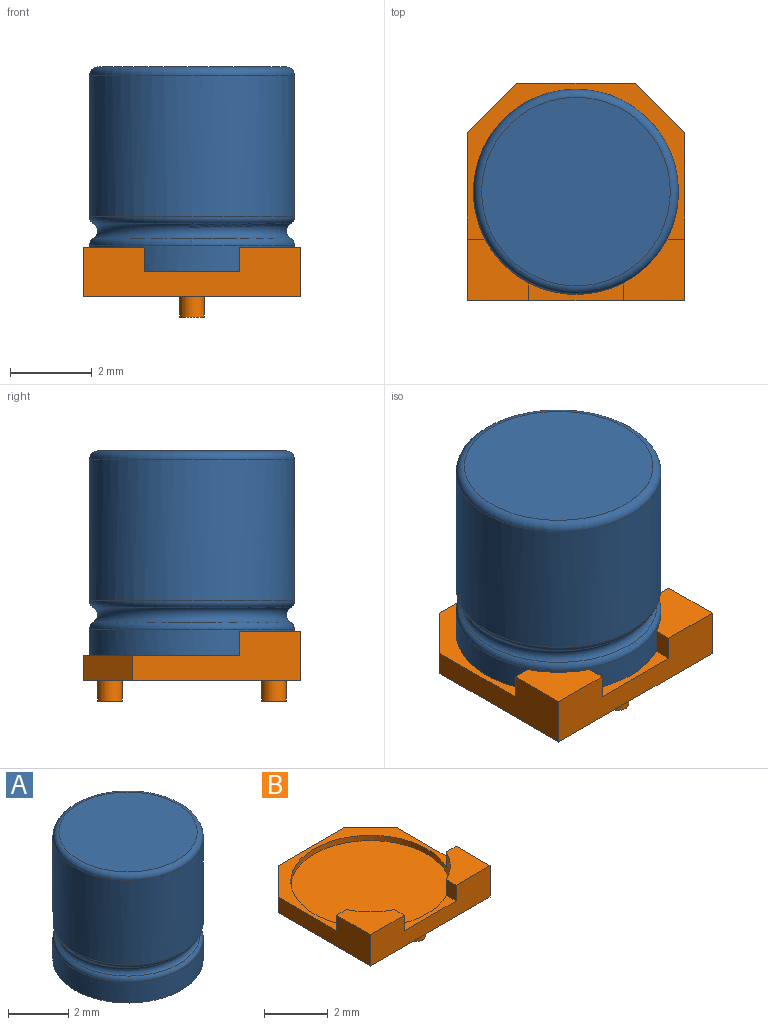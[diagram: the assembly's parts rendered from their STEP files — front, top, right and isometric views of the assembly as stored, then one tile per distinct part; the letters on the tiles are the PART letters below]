
ASSEMBLY  parts=2 mates=1
PART A: 8 faces, bbox 5.4x5.4x5.2 mm
  f0: plane 5x5mm, normal (0,0,-1), area 19.6mm2, adj f1
  f1: cylinder r=2.5mm len=5mm, axis (0,0,1), area 13.4mm2, adj f0,f5
  f2: torus R=2.5mm, axis (0,0,1), area 6.1mm2, adj f5,f6
  f3: cylinder r=2.5mm len=5mm, axis (0,0,1), area 54.2mm2, adj f6,f7
  f4: plane 4.6x4.6mm, normal (0,0,1), area 16.6mm2, adj f7
  f5: torus R=2.3mm, axis (0,0,-1), area 3.2mm2, adj f1,f2
  f6: torus R=2.3mm, axis (0,0,-1), area 3.2mm2, adj f2,f3
  f7: torus R=2.3mm, axis (0,0,1), area 4.8mm2, adj f3,f4
PART B: 21 faces, bbox 5.3x5.3x1.7 mm
  f0: plane 5.3x3.8mm, normal (0,0,1), area 3.3mm2, adj f2,f3,f4,f6,f7,f9,f11,f15
  f1: plane 2.3x0.43mm, normal (0,0,1), area 0.6mm2, adj f5,f9,f12,f14
  f2: plane 2.9x0.6mm, normal (0,1,0), area 1.7mm2, adj f0,f3,f7,f8
  f3: plane 1.2x1.2mm, normal (-0.71,0.71,0), area 1mm2, adj f0,f2,f4,f8
  f4: plane 4.1x1.2mm, normal (-1,0,0), area 3.4mm2, adj f0,f3,f5,f8,f11,f13
  f5: plane 5.3x1.2mm, normal (0,-1,0), area 5mm2, adj f1,f4,f6,f8,f12,f13,f14,f16
  f6: plane 4.1x1.2mm, normal (1,0,0), area 3.4mm2, adj f0,f5,f7,f8,f15,f16
  f7: plane 1.2x1.2mm, normal (0.71,0.71,0), area 1mm2, adj f0,f2,f6,f8
  f8: plane 5.3x5.3mm, normal (0,0,-1), area 26.1mm2, adj f2,f3,f4,f5,f6,f7,f17,f19
  f9: cylinder r=2.5mm len=5mm, axis (0,0,1), area 5mm2, adj f0,f1,f10,f11,f12,f13,f14,f15
  f10: plane 5x5mm, normal (0,0,1), area 19.6mm2, adj f9
  f11: plane 0.6x0.43mm, normal (0,1,0), area 0.3mm2, adj f0,f4,f9,f13
  f12: plane 0.6x0.43mm, normal (1,0,0), area 0.3mm2, adj f1,f5,f9,f13
  f13: plane 1.5x1.5mm, normal (0,0,1), area 1.6mm2, adj f4,f5,f9,f11,f12
  f14: plane 0.6x0.43mm, normal (-1,0,0), area 0.3mm2, adj f1,f5,f9,f16
  f15: plane 0.6x0.43mm, normal (0,1,0), area 0.3mm2, adj f0,f6,f9,f16
  f16: plane 1.5x1.5mm, normal (0,0,1), area 1.6mm2, adj f5,f6,f9,f14,f15
  f17: cylinder r=0.3mm len=0.6mm, axis (0,0,1), area 0.9mm2, adj f8,f18
  f18: plane 0.6x0.6mm, normal (0,0,-1), area 0.3mm2, adj f17
  f19: cylinder r=0.3mm len=0.6mm, axis (0,0,1), area 0.9mm2, adj f8,f20
  f20: plane 0.6x0.6mm, normal (0,0,-1), area 0.3mm2, adj f19
PLACE A t=(-1.12,-0.55,0.19)mm
PLACE B t=(-1.12,-0.55,-0.21)mm fixed
MATE fastened A.f1 <-> B.f9  axis (0,0,-1) through (-1.12,-0.55,0.19)mm
